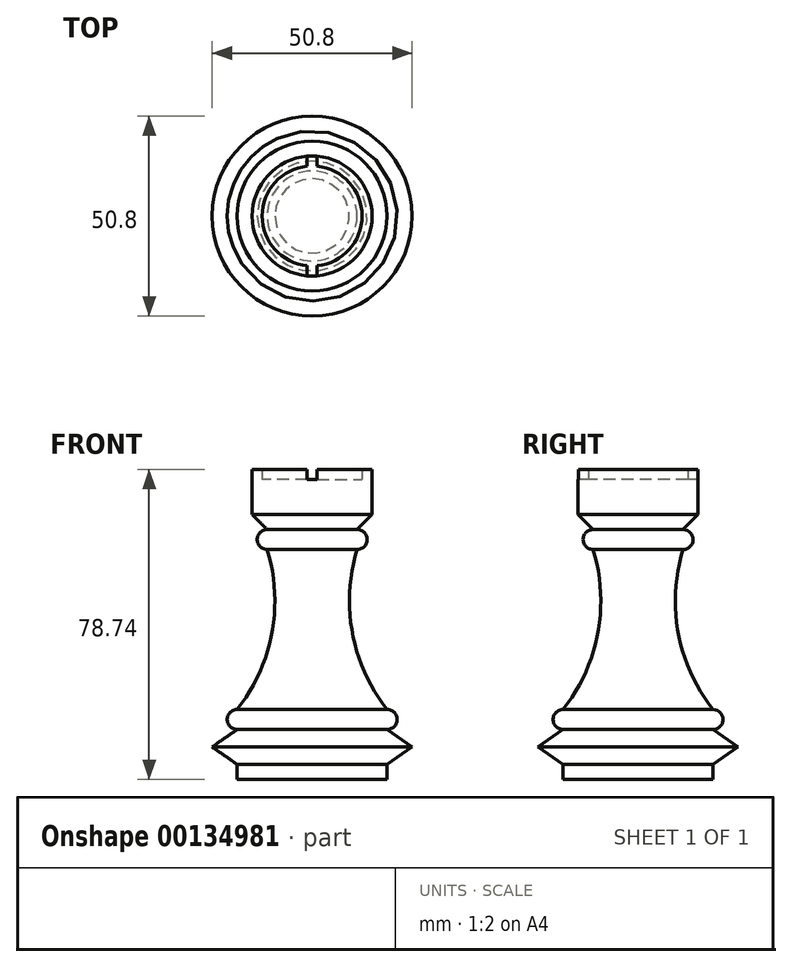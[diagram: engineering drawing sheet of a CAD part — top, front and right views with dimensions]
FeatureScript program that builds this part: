
annotation { "Feature Type Name" : "Feature", "Feature Type Description" : "" }
export const myFeature = defineFeature(function(context is Context, id is Id, definition is map)
    precondition{}
    {
        {
            var Q0;
            Q0=qCreatedBy(makeId("Front.planeOp"),FACE);
            var sketch = newSketch(context, id + "F0", { "sketchPlane" : qUnion([Q0])});
            skLineSegment(sketch, "E0", {"start": v(0, 0) * mm, "end": v(19.05, 0) * mm});
            skLineSegment(sketch, "E1", {"start": v(19.05, 0) * mm, "end": v(19.05, 3.8) * mm});
            skLineSegment(sketch, "E2", {"start": v(19.05, 3.8) * mm, "end": v(25.4, 8.25) * mm});
            skLineSegment(sketch, "E3", {"start": v(25.4, 8.26) * mm, "end": v(19.05, 12.7) * mm});
            skLineSegment(sketch, "E4", {"start": v(0, 0) * mm, "end": v(0, 76.2) * mm});
            skLineSegment(sketch, "E5", {"start": v(0, 76.2) * mm, "end": v(12.7, 76.2) * mm});
            skLineSegment(sketch, "E6", {"start": v(12.7, 76.2) * mm, "end": v(12.7, 78.74) * mm});
            skLineSegment(sketch, "E7", {"start": v(15.24, 78.74) * mm, "end": v(15.24, 67.31) * mm});
            skLineSegment(sketch, "E8", {"start": v(15.24, 67.31) * mm, "end": v(11.43, 63.5) * mm});
            skLineSegment(sketch, "E9", {"start": v(12.7, 78.74) * mm, "end": v(15.24, 78.74) * mm});
            skArc(sketch, "E10", {"start": v(11.43, 58.42) * mm, "mid": v(13.97, 60.96) * mm, "end": v(11.43, 63.5) * mm});
            skArc(sketch, "E11", {"start": v(19.05, 12.7) * mm, "mid": v(21.59, 15.24) * mm, "end": v(19.05, 17.78) * mm});
            skArc(sketch, "E12", {"start": v(11.43, 58.42) * mm, "mid": v(10.23, 37.16) * mm, "end": v(19.05, 17.78) * mm});
            skSolve(sketch);
        }
        {
            var Q0;
            Q0 = qSketchRegion(id + "F0", true);
            var Q1;
            Q1=sQuery(id+"F0.wireOp",EDGE,"E4");
            revolve(context, id + "F1", {"entities" : qUnion([Q0]), "axis" : qUnion([Q1]), "revolveType" : RevolveType.FULL});
        }
        {
            var Q0;
            Q0=qCreatedBy(makeId("Front.planeOp"),FACE);
            var sketch = newSketch(context, id + "F2", { "sketchPlane" : qUnion([Q0])});
            skLineSegment(sketch, "E13.bottom", {"start": v(1.27, 78.74) * mm, "end": v(-1.27, 78.74) * mm});
            skLineSegment(sketch, "E13.top", {"start": v(1.27, 76.2) * mm, "end": v(-1.27, 76.2) * mm});
            skLineSegment(sketch, "E13.left", {"start": v(1.27, 78.74) * mm, "end": v(1.27, 76.2) * mm});
            skLineSegment(sketch, "E13.right", {"start": v(-1.27, 78.74) * mm, "end": v(-1.27, 76.2) * mm});
            skPoint(sketch, "E13.middle", {"position": v(0, 77.47) * mm});
            skSolve(sketch);
        }
        {
            var Q0;
            Q0 = qSketchRegion(id + "F2", true);
            extrude(context, id + "F3", {"entities" : qUnion([Q0]), "operationType" : NewBodyOperationType.REMOVE, "endBound" : BoundingType.THROUGH_ALL, "oppositeDirection" : true, "depth" : 25.4 * mm, "hasSecondDirection" : true, "secondDirectionOppositeDirection" : false, "secondDirectionDepth" : 25.4 * mm});
        }
    });
